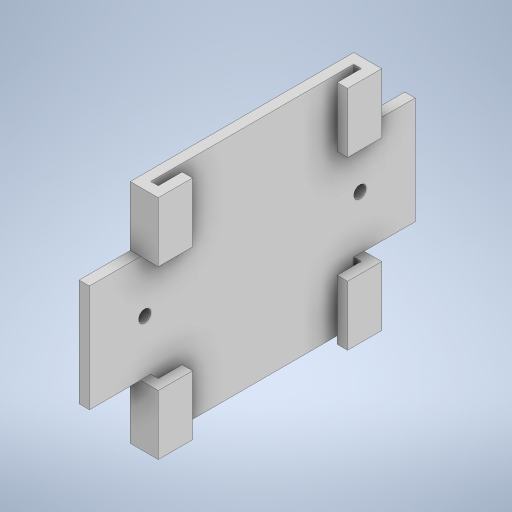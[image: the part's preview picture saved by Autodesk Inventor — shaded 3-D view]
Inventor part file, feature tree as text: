
AUTODESK INVENTOR PART (.ipt)
format: ipt  version: 2024.3 (Build 283343000, 343)  size: 285,184 bytes
history: native  units: in
note: dims shown in document units (in); Inventor stores cm internally (conversion verified against a paired STEP export)
features: extrude x4, sketch x4
ambient origin geometry x8: Origin, YZ Plane, XZ Plane, XY Plane, X Axis, Y Axis, Z Axis, Center Point
bodies: Solid1 (feature_tree)
feature tree (8):
  extrude  "Extrusion1"  Depth=0.2677in
  extrude  "Extrusion2"  Depth=0.0984in
  extrude  "Extrusion3"  Depth=0.0709in
  extrude  "Extrusion4"  Depth=0.2283in
  sketch  "Sketch1"  dims[d0=2.1339in d1=0.2677in]
  sketch  "Sketch2"  dims[d2=0.3268in d3=0.0984in]
  sketch  "Sketch3"  dims[d4=0.2283in d5=0.0709in]
  sketch  "Sketch4"  dims[d6=0.3268in d7=0.2283in d8=0.5709in d9=0.0in d10=1.5551in d11=1.5551in d12=1.0236in d13=0.0in d14=0.5709in d15=0.0in d16=0.5276in d17=0.1181in d18=0.5276in d19=0.1181in d20=0.1772in d21=0.0in]
